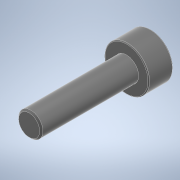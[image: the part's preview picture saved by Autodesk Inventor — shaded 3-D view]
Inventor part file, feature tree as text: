
AUTODESK INVENTOR PART (.ipt)
format: ipt  version: 2022 (Build 260153000, 153)  size: 137,216 bytes
history: native  units: in
note: dims shown in document units (in); Inventor stores cm internally (conversion verified against a paired STEP export)
features: sketch x3, extrude x2, fillet x1, chamfer x1
ambient origin geometry x8: Origin, YZ Plane, XZ Plane, XY Plane, X Axis, Y Axis, Z Axis, Center Point
bodies: Body1 (feature_tree)
feature tree (7):
  extrude  "Extrusion2"  Depth=0.4724in TaperAngle=0.0deg
  extrude  "Extrusion1"  Depth=0.0039in
  fillet  "Fillet1"  Radius=0.0039in
  chamfer  "Chamfer1"  Distance=0.0079in
  sketch  "Sketch1"  dims[d0=0.1181in d1=0.0in d2=0.4724in d3=0.0in]
  sketch  "Sketch2"  dims[d4=0.1181in d5=0.0in d6=0.0039in d7=0.0039in d8=0.0079in d9=0.0079in d10=17.7165in]
  sketch  "Sketch3"
